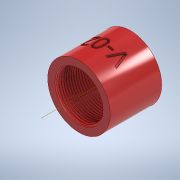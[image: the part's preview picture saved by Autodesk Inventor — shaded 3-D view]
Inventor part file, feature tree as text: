
AUTODESK INVENTOR PART (.ipt)
format: ipt  version: 2021.1 (Build 251245000, 245)  size: 784,384 bytes
history: native  units: in
note: dims shown in document units (in); Inventor stores cm internally (conversion verified against a paired STEP export)
features: sketch x4, extrude x2, plane x2, helix x1, emboss x1
ambient origin geometry x8: Origin, YZ Plane, XZ Plane, XY Plane, X Axis, Y Axis, Z Axis, Center Point
bodies: Body1 (feature_tree)
feature tree (10):
  extrude  "Extrusion3"  Depth=2.125in
  extrude  "Extrusion4"  Depth=1.6368in
  helix  "Coil2"  [1 undecoded]
  plane  "Work Plane1"
  plane  "Work Plane2"
  emboss  "Emboss1"
  sketch  "Sketch3"  dims[d8=0.635in d9=2.125in]
  sketch  "Sketch4"  dims[d10=1.75in d11=0.0in d12=1.6368in d13=1.25in]
  sketch  "Sketch5"  dims[d14=0.0in]
  sketch  "Sketch7"  dims[d15=60.0deg d17=0.0045in d18=0.7719in d27=0.0in d28=0.0833in d29=1.25in d30=0.3937in d31=0.0in d32=90.0deg d33=90.0deg d34=0.0in d35=0.0in d36=1.0625in d48=1.0625in d49=0.1in d50=0.0in]
note: 1 required parameter value undecoded (feature->parameter linkage not recoverable at this tier; creation-order binding heuristic only, values carry confidence <= 0.55)
